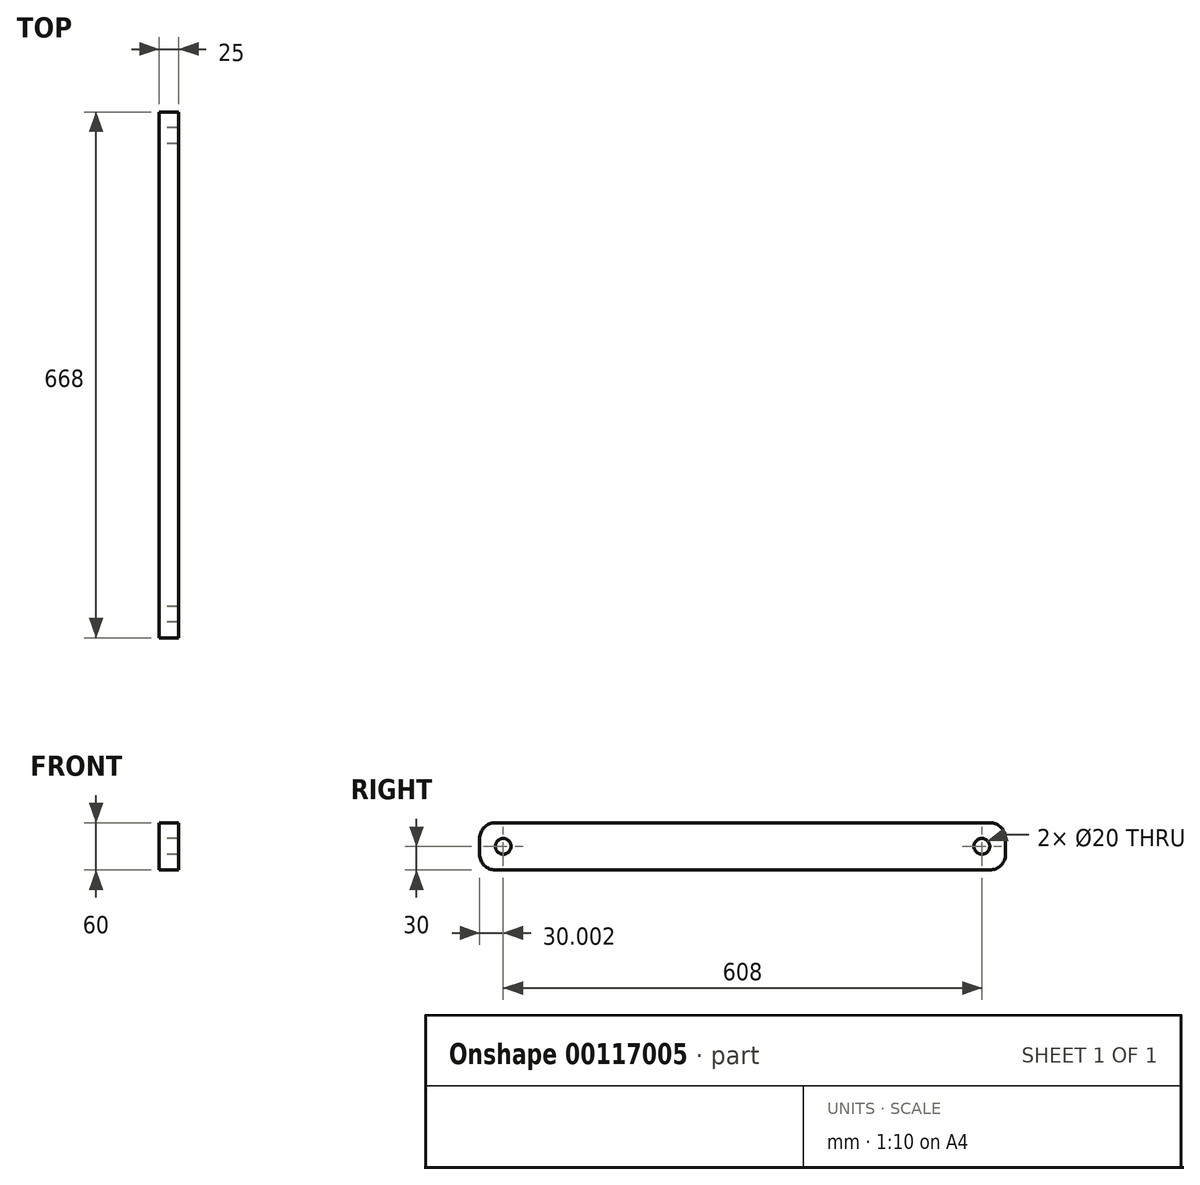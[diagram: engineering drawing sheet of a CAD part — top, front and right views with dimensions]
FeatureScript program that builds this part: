
annotation { "Feature Type Name" : "Feature", "Feature Type Description" : "" }
export const myFeature = defineFeature(function(context is Context, id is Id, definition is map)
    precondition{}
    {
        {
            var Q0;
            Q0=qCreatedBy(makeId("Right.planeOp"),FACE);
            var sketch = newSketch(context, id + "F0", { "sketchPlane" : qUnion([Q0])});
            skCircle(sketch, "E0", {"center": v(-56.47, 0) * mm, "radius": 10 * mm});
            skCircle(sketch, "E1", {"center": v(551.53, 0) * mm, "radius": 10 * mm});
            skLineSegment(sketch, "E2.bottom", {"start": v(581.53, 30) * mm, "end": v(-86.47, 30) * mm});
            skLineSegment(sketch, "E2.top", {"start": v(581.53, -30) * mm, "end": v(-86.47, -30) * mm});
            skLineSegment(sketch, "E2.left", {"start": v(581.53, 30) * mm, "end": v(581.53, -30) * mm});
            skLineSegment(sketch, "E2.right", {"start": v(-86.47, 30) * mm, "end": v(-86.47, -30) * mm});
            skSolve(sketch);
        }
        {
            var Q0;
            Q0=makeQuery(id+"F0.imprint","IMPRINT",FACE,{"disambiguationData":[TD([[makeQuery(id+"F0.imprint","IMPRINT",EDGE,{"derivedFrom":sQuery(id+"F0.wireOp",EDGE,"E0")}),-1.0]])]});
            extrude(context, id + "F1", {"entities" : qUnion([Q0]), "depth" : 25 * mm, "offsetDistance" : 25 * mm});
        }
        {
            var Q0;
            Q0=makeQuery(id+"F1.opExtrude","SWEPT_EDGE",EDGE,{"disambiguationData":[OSD([sQuery(id+"F0.wireOp",EDGE,"E2.bottom"),sQuery(id+"F0.wireOp",EDGE,"E2.left")])]});
            fillet(context, id + "F2", {"entities" : qUnion([Q0]), "radius" : 20 * mm, "tangentPropagation" : true, "allowEdgeOverflow" : false});
        }
        {
            var Q0;
            Q0=makeQuery(id+"F1.opExtrude","SWEPT_EDGE",EDGE,{"disambiguationData":[OSD([sQuery(id+"F0.wireOp",EDGE,"E2.top"),sQuery(id+"F0.wireOp",EDGE,"E2.left")])]});
            fillet(context, id + "F3", {"entities" : qUnion([Q0]), "radius" : 20 * mm, "tangentPropagation" : true, "allowEdgeOverflow" : false});
        }
        {
            var Q0;
            Q0=makeQuery(id+"F1.opExtrude","SWEPT_EDGE",EDGE,{"disambiguationData":[OSD([sQuery(id+"F0.wireOp",EDGE,"E2.bottom"),sQuery(id+"F0.wireOp",EDGE,"E2.right")])]});
            fillet(context, id + "F4", {"entities" : qUnion([Q0]), "radius" : 20 * mm, "tangentPropagation" : true, "allowEdgeOverflow" : false});
        }
        {
            var Q0;
            Q0=makeQuery(id+"F1.opExtrude","SWEPT_EDGE",EDGE,{"disambiguationData":[OSD([sQuery(id+"F0.wireOp",EDGE,"E2.top"),sQuery(id+"F0.wireOp",EDGE,"E2.right")])]});
            fillet(context, id + "F5", {"entities" : qUnion([Q0]), "radius" : 20 * mm, "tangentPropagation" : true, "allowEdgeOverflow" : false});
        }
    });
